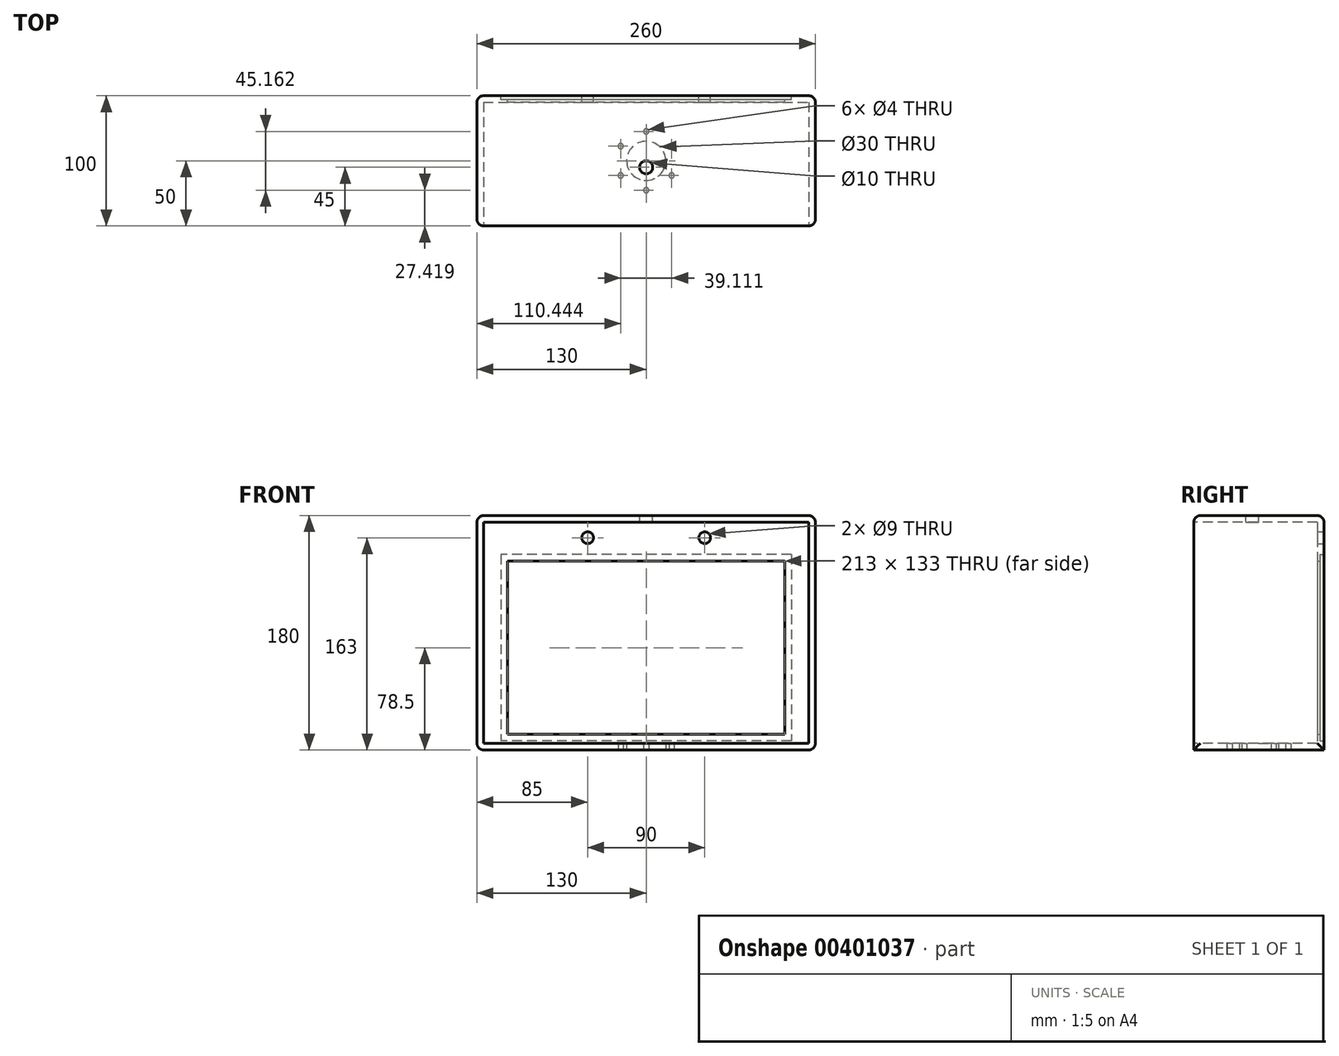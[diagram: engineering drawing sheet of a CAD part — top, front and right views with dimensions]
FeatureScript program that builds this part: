
annotation { "Feature Type Name" : "Feature", "Feature Type Description" : "" }
export const myFeature = defineFeature(function(context is Context, id is Id, definition is map)
    precondition{}
    {
        {
            var Q0;
            Q0=qCreatedBy(makeId("Top.planeOp"),FACE);
            var sketch = newSketch(context, id + "F0", { "sketchPlane" : qUnion([Q0])});
            skLineSegment(sketch, "E0.bottom", {"start": v(-130, 50) * mm, "end": v(130, 50) * mm});
            skLineSegment(sketch, "E0.top", {"start": v(-130, -50) * mm, "end": v(130, -50) * mm});
            skLineSegment(sketch, "E0.left", {"start": v(-130, 50) * mm, "end": v(-130, -50) * mm});
            skLineSegment(sketch, "E0.right", {"start": v(130, 50) * mm, "end": v(130, -50) * mm});
            skSolve(sketch);
        }
        {
            var Q0;
            Q0=makeQuery(id+"F0.imprint","IMPRINT",FACE,{"disambiguationData":[TD([[makeQuery(id+"F0.imprint","IMPRINT",EDGE,{"derivedFrom":sQuery(id+"F0.wireOp",EDGE,"E0.bottom")}),-1.0]])]});
            extrude(context, id + "F1", {"entities" : qUnion([Q0]), "depth" : 180 * mm});
        }
        {
            var Q0;
            Q0=makeQuery(id+"F1.opExtrude","SWEPT_FACE",FACE,{"disambiguationData":[OSD([sQuery(id+"F0.wireOp",EDGE,"E0.top")])]});
            shell(context, id + "F2", {"entities" : qUnion([Q0]), "thickness" : 5 * mm});
        }
        {
            var Q0;
            Q0=makeQuery(id+"F1.opExtrude","SWEPT_FACE",FACE,{"disambiguationData":[OSD([sQuery(id+"F0.wireOp",EDGE,"E0.bottom")])]});
            var sketch = newSketch(context, id + "F3", { "sketchPlane" : qUnion([Q0])});
            skLineSegment(sketch, "E1.bottom", {"start": v(-111.5, 150) * mm, "end": v(111.5, 150) * mm});
            skLineSegment(sketch, "E1.top", {"start": v(-111.5, 7) * mm, "end": v(111.5, 7) * mm});
            skLineSegment(sketch, "E1.left", {"start": v(-111.5, 150) * mm, "end": v(-111.5, 7) * mm});
            skLineSegment(sketch, "E1.right", {"start": v(111.5, 150) * mm, "end": v(111.5, 7) * mm});
            skLineSegment(sketch, "E2.0", {"start": v(-106.5, 145) * mm, "end": v(-106.5, 12) * mm});
            skLineSegment(sketch, "E2.1", {"start": v(-106.5, 145) * mm, "end": v(106.5, 145) * mm});
            skLineSegment(sketch, "E2.2", {"start": v(106.5, 145) * mm, "end": v(106.5, 12) * mm});
            skLineSegment(sketch, "E2.3", {"start": v(-106.5, 12) * mm, "end": v(106.5, 12) * mm});
            skCircle(sketch, "E3", {"center": v(-45, 163) * mm, "radius": 4.5 * mm});
            skCircle(sketch, "E4", {"center": v(45, 163) * mm, "radius": 4.5 * mm});
            skSolve(sketch);
        }
        {
            var Q0;
            Q0=makeQuery(id+"F3.imprint","IMPRINT",FACE,{"disambiguationData":[TD([[makeQuery(id+"F3.imprint","IMPRINT",EDGE,{"derivedFrom":sQuery(id+"F3.wireOp",EDGE,"E1.bottom")}),-1.0]])]});
            extrude(context, id + "F4", {"entities" : qUnion([Q0]), "operationType" : NewBodyOperationType.REMOVE, "oppositeDirection" : true, "depth" : 3 * mm});
        }
        {
            var Q0;
            Q0=makeQuery(id+"F4.boolean.opBoolean","SPLIT",FACE,{"disambiguationData":[TD([makeQuery(id+"F4.opExtrude","SWEPT_FACE",FACE,{"disambiguationData":[OSD([sQuery(id+"F3.wireOp",EDGE,"E2.0")])]})])],"derivedFrom":makeQuery(id+"F1.opExtrude","SWEPT_FACE",FACE,{"disambiguationData":[OSD([sQuery(id+"F0.wireOp",EDGE,"E0.bottom")])]})});
            extrude(context, id + "F5", {"entities" : qUnion([Q0]), "operationType" : NewBodyOperationType.REMOVE, "oppositeDirection" : true, "depth" : 25 * mm});
        }
        {
            var Q0;
            Q0=makeQuery(id+"F3.imprint","IMPRINT",FACE,{"disambiguationData":[TD([[makeQuery(id+"F3.imprint","IMPRINT",EDGE,{"derivedFrom":sQuery(id+"F3.wireOp",EDGE,"E3")}),1.0]])]});
            var Q1;
            Q1=makeQuery(id+"F3.imprint","IMPRINT",FACE,{"disambiguationData":[TD([[makeQuery(id+"F3.imprint","IMPRINT",EDGE,{"derivedFrom":sQuery(id+"F3.wireOp",EDGE,"E4")}),1.0]])]});
            extrude(context, id + "F6", {"entities" : qUnion([Q0, Q1]), "operationType" : NewBodyOperationType.REMOVE, "oppositeDirection" : true, "depth" : 25 * mm});
        }
        {
            var Q0;
            Q0=makeQuery(id+"F1.opExtrude","CAP_FACE",FACE,{"disambiguationData":[OSD([sQuery(id+"F0.wireOp",EDGE,"E0.bottom"),sQuery(id+"F0.wireOp",EDGE,"E0.top"),sQuery(id+"F0.wireOp",EDGE,"E0.left"),sQuery(id+"F0.wireOp",EDGE,"E0.right")])],"isStart":true});
            var sketch = newSketch(context, id + "F7", { "sketchPlane" : qUnion([Q0])});
            skCircle(sketch, "E5", {"center": v(0, 22.58) * mm, "radius": 2 * mm});
            skCircle(sketch, "E6.1.0", {"center": v(-19.56, 11.3) * mm, "radius": 2 * mm});
            skCircle(sketch, "E6.2.0", {"center": v(-19.56, -11.3) * mm, "radius": 2 * mm});
            skCircle(sketch, "E6.3.0", {"center": v(0, -22.58) * mm, "radius": 2 * mm});
            skCircle(sketch, "E6.4.0", {"center": v(19.56, -11.3) * mm, "radius": 2 * mm});
            skCircle(sketch, "E6.5.0", {"center": v(19.56, 11.3) * mm, "radius": 2 * mm});
            skPoint(sketch, "E6.center", {"position": v(0, 0) * mm});
            skCircle(sketch, "E7", {"center": v(0, 0) * mm, "radius": 15 * mm});
            skSolve(sketch);
        }
        {
            var Q0;
            Q0=makeQuery(id+"F7.imprint","IMPRINT",FACE,{"disambiguationData":[TD([[makeQuery(id+"F7.imprint","IMPRINT",EDGE,{"derivedFrom":sQuery(id+"F7.wireOp",EDGE,"E6.1.0")}),1.0]])]});
            var Q1;
            Q1=makeQuery(id+"F7.imprint","IMPRINT",FACE,{"disambiguationData":[TD([[makeQuery(id+"F7.imprint","IMPRINT",EDGE,{"derivedFrom":sQuery(id+"F7.wireOp",EDGE,"E5")}),1.0]])]});
            var Q2;
            Q2=makeQuery(id+"F7.imprint","IMPRINT",FACE,{"disambiguationData":[TD([[makeQuery(id+"F7.imprint","IMPRINT",EDGE,{"derivedFrom":sQuery(id+"F7.wireOp",EDGE,"E6.5.0")}),1.0]])]});
            var Q3;
            Q3=makeQuery(id+"F7.imprint","IMPRINT",FACE,{"disambiguationData":[TD([[makeQuery(id+"F7.imprint","IMPRINT",EDGE,{"derivedFrom":sQuery(id+"F7.wireOp",EDGE,"E6.4.0")}),1.0]])]});
            var Q4;
            Q4=makeQuery(id+"F7.imprint","IMPRINT",FACE,{"disambiguationData":[TD([[makeQuery(id+"F7.imprint","IMPRINT",EDGE,{"derivedFrom":sQuery(id+"F7.wireOp",EDGE,"E6.3.0")}),1.0]])]});
            var Q5;
            Q5=makeQuery(id+"F7.imprint","IMPRINT",FACE,{"disambiguationData":[TD([[makeQuery(id+"F7.imprint","IMPRINT",EDGE,{"derivedFrom":sQuery(id+"F7.wireOp",EDGE,"E6.2.0")}),1.0]])]});
            var Q6;
            Q6=makeQuery(id+"F7.imprint","IMPRINT",FACE,{"disambiguationData":[TD([[makeQuery(id+"F7.imprint","IMPRINT",EDGE,{"derivedFrom":sQuery(id+"F7.wireOp",EDGE,"E7")}),1.0]])]});
            extrude(context, id + "F8", {"entities" : qUnion([Q0, Q1, Q2, Q3, Q4, Q5, Q6]), "operationType" : NewBodyOperationType.REMOVE, "oppositeDirection" : true, "depth" : 25 * mm});
        }
        {
            var Q0;
            Q0=makeQuery(id+"F1.opExtrude","CAP_EDGE",EDGE,{"disambiguationData":[OSD([sQuery(id+"F0.wireOp",EDGE,"E0.bottom")])],"isStart":false});
            var Q1;
            Q1=makeQuery(id+"F1.opExtrude","CAP_EDGE",EDGE,{"disambiguationData":[OSD([sQuery(id+"F0.wireOp",EDGE,"E0.left")])],"isStart":false});
            var Q2;
            Q2=makeQuery(id+"F1.opExtrude","SWEPT_EDGE",EDGE,{"disambiguationData":[OSD([sQuery(id+"F0.wireOp",EDGE,"E0.bottom"),sQuery(id+"F0.wireOp",EDGE,"E0.left")])]});
            var Q3;
            Q3=makeQuery(id+"F1.opExtrude","SWEPT_FACE",FACE,{"disambiguationData":[OSD([sQuery(id+"F0.wireOp",EDGE,"E0.left")])]});
            var Q4;
            Q4=makeQuery(id+"F1.opExtrude","CAP_FACE",FACE,{"disambiguationData":[OSD([sQuery(id+"F0.wireOp",EDGE,"E0.bottom"),sQuery(id+"F0.wireOp",EDGE,"E0.top"),sQuery(id+"F0.wireOp",EDGE,"E0.left"),sQuery(id+"F0.wireOp",EDGE,"E0.right")])],"isStart":false});
            var Q5;
            Q5=makeQuery(id+"F1.opExtrude","SWEPT_FACE",FACE,{"disambiguationData":[OSD([sQuery(id+"F0.wireOp",EDGE,"E0.right")])]});
            fillet(context, id + "F9", {"entities" : qUnion([Q0, Q1, Q2, Q3, Q4, Q5]), "radius" : 5 * mm, "tangentPropagation" : true, "allowEdgeOverflow" : false});
        }
        {
            var Q0;
            Q0=makeQuery(id+"F1.opExtrude","CAP_FACE",FACE,{"disambiguationData":[OSD([sQuery(id+"F0.wireOp",EDGE,"E0.bottom"),sQuery(id+"F0.wireOp",EDGE,"E0.top"),sQuery(id+"F0.wireOp",EDGE,"E0.left"),sQuery(id+"F0.wireOp",EDGE,"E0.right")])],"isStart":false});
            var sketch = newSketch(context, id + "F10", { "sketchPlane" : qUnion([Q0])});
            skCircle(sketch, "E8", {"center": v(0, -5) * mm, "radius": 5 * mm});
            skSolve(sketch);
        }
        {
            var Q0;
            Q0=makeQuery(id+"F10.imprint","IMPRINT",FACE,{"disambiguationData":[TD([[makeQuery(id+"F10.imprint","IMPRINT",EDGE,{"derivedFrom":sQuery(id+"F10.wireOp",EDGE,"E8")}),1.0]])]});
            extrude(context, id + "F11", {"entities" : qUnion([Q0]), "operationType" : NewBodyOperationType.REMOVE, "oppositeDirection" : true, "depth" : 25 * mm, "offsetDistance" : 25 * mm});
        }
    });
